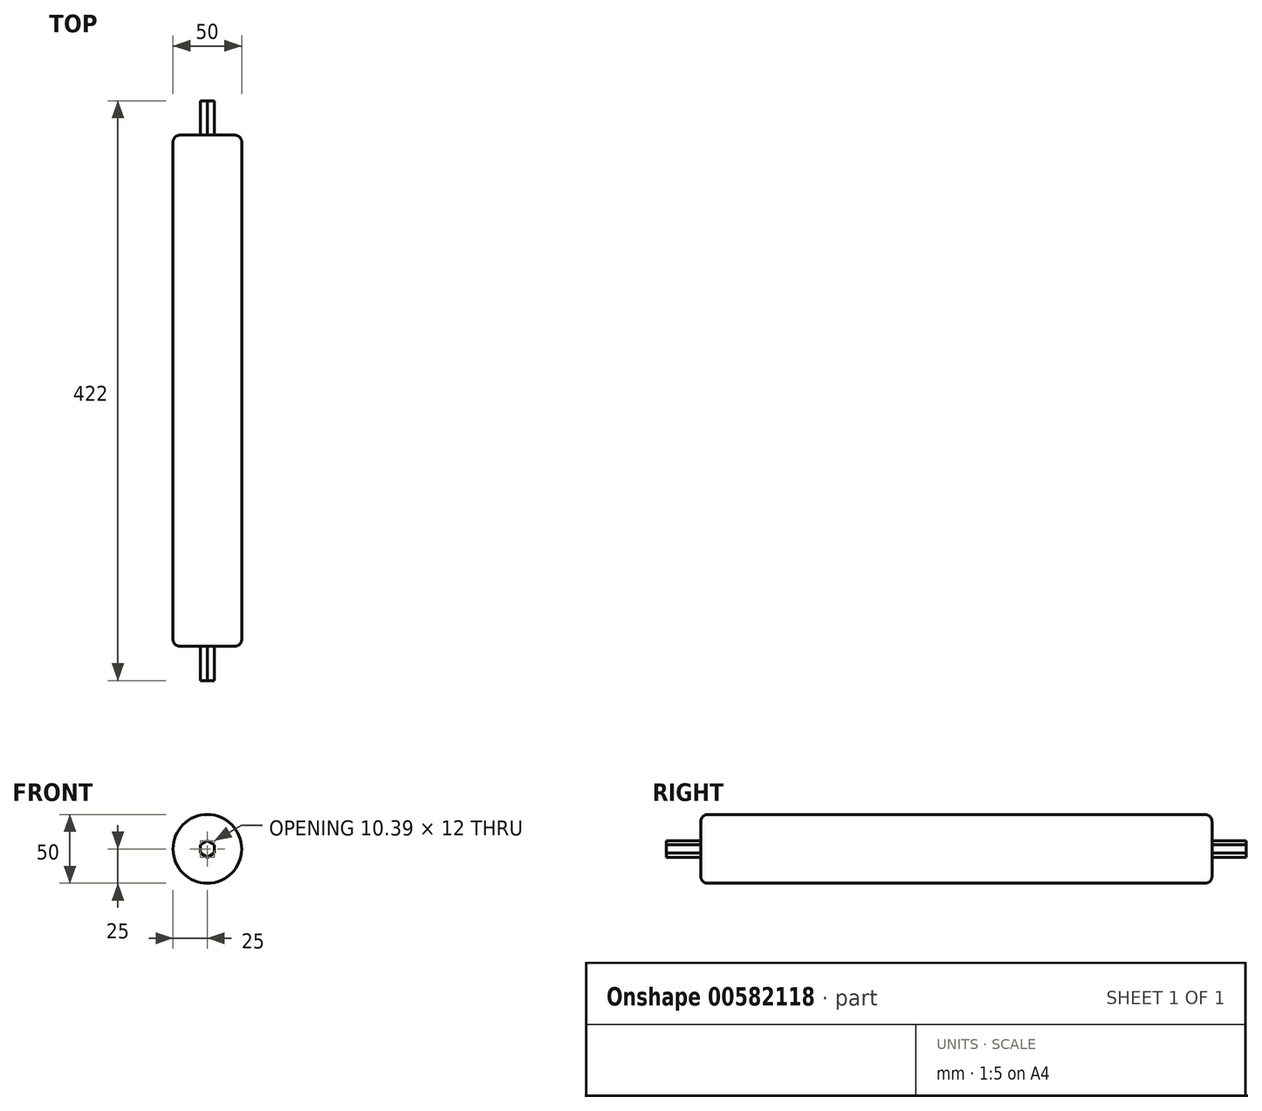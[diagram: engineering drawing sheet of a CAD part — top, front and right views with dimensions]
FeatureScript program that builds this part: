
annotation { "Feature Type Name" : "Feature", "Feature Type Description" : "" }
export const myFeature = defineFeature(function(context is Context, id is Id, definition is map)
    precondition{}
    {
        {
            var Q0;
            Q0=qCreatedBy(makeId("Front.planeOp"),FACE);
            var sketch = newSketch(context, id + "F0", { "sketchPlane" : qUnion([Q0])});
            skCircle(sketch, "E0", {"center": v(0, 0) * mm, "radius": 25 * mm});
            skSolve(sketch);
        }
        {
            var Q0;
            Q0=makeQuery(id+"F0.imprint","IMPRINT",FACE,{"disambiguationData":[TD([[makeQuery(id+"F0.imprint","IMPRINT",EDGE,{"derivedFrom":sQuery(id+"F0.wireOp",EDGE,"E0")}),1.0]])]});
            extrude(context, id + "F1", {"entities" : qUnion([Q0]), "depth" : 372 * mm, "offsetDistance" : 25 * mm});
        }
        {
            var Q0;
            Q0=makeQuery(id+"F1.opExtrude","CAP_EDGE",EDGE,{"disambiguationData":[OSD([sQuery(id+"F0.wireOp",EDGE,"E0")])],"isStart":false});
            var Q1;
            Q1=makeQuery(id+"F1.opExtrude","CAP_EDGE",EDGE,{"disambiguationData":[OSD([sQuery(id+"F0.wireOp",EDGE,"E0")])],"isStart":true});
            fillet(context, id + "F2", {"entities" : qUnion([Q0, Q1]), "radius" : 5 * mm, "tangentPropagation" : true, "allowEdgeOverflow" : false});
        }
        {
            var Q0;
            Q0=makeQuery(id+"F1.opExtrude","CAP_FACE",FACE,{"disambiguationData":[OSD([sQuery(id+"F0.wireOp",EDGE,"E0")])],"isStart":true});
            var sketch = newSketch(context, id + "F3", { "sketchPlane" : qUnion([Q0])});
            skCircle(sketch, "E1.cCircle", {"center": v(0, 0) * mm, "radius": 5.2 * mm, "construction": true});
            skLineSegment(sketch, "E1.0", {"start": v(5.2, -3) * mm, "end": v(0, -6) * mm});
            skLineSegment(sketch, "E1.1", {"start": v(0, -6) * mm, "end": v(-5.2, -3) * mm});
            skLineSegment(sketch, "E1.2", {"start": v(-5.2, -3) * mm, "end": v(-5.2, 3) * mm});
            skLineSegment(sketch, "E1.3", {"start": v(-5.2, 3) * mm, "end": v(0, 6) * mm});
            skLineSegment(sketch, "E1.4", {"start": v(0, 6) * mm, "end": v(5.2, 3) * mm});
            skLineSegment(sketch, "E1.5", {"start": v(5.2, 3) * mm, "end": v(5.2, -3) * mm});
            skPoint(sketch, "E1.0.midPoint", {"position": v(2.6, -4.5) * mm});
            skSolve(sketch);
        }
        {
            var Q0;
            Q0 = qSketchRegion(id + "F3", true);
            extrude(context, id + "F4", {"entities" : qUnion([Q0]), "operationType" : NewBodyOperationType.ADD, "depth" : 25 * mm, "offsetDistance" : 25 * mm, "hasSecondDirection" : true, "secondDirectionOppositeDirection" : true, "secondDirectionDepth" : 397 * mm});
        }
    });
